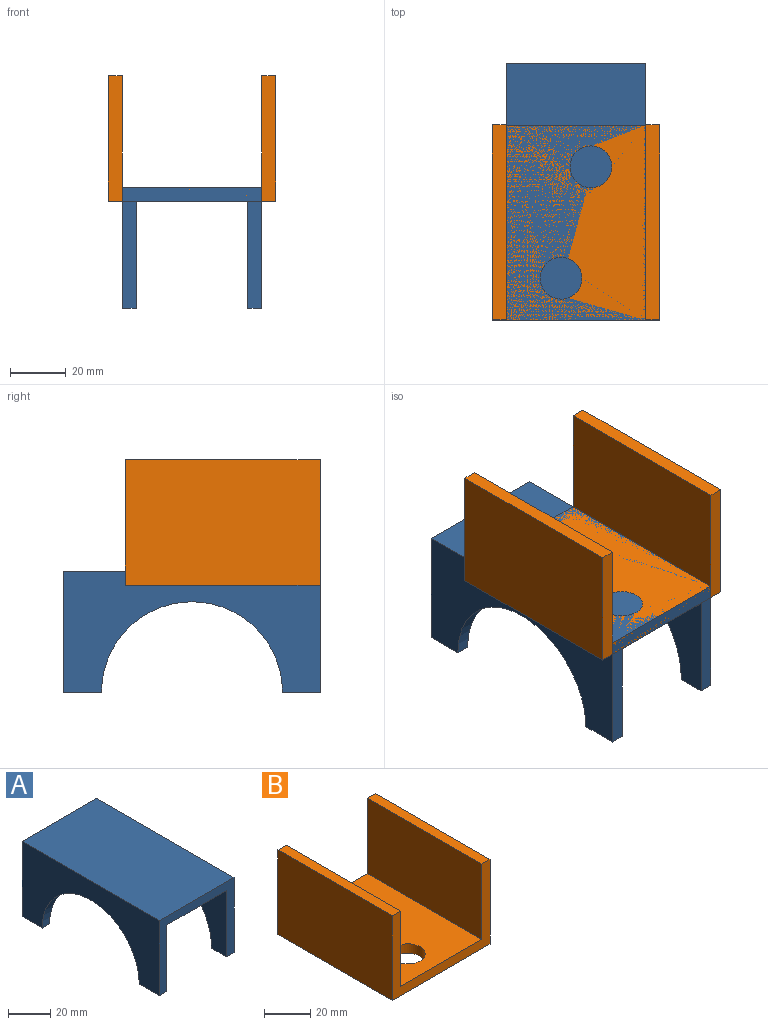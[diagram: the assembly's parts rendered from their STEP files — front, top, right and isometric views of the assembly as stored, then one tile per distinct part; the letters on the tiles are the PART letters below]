
ASSEMBLY  parts=2 mates=1
PART A: 14 faces, bbox 50x92x43.5 mm
  f0: plane 13.5x5mm, normal (0,0,-1), area 67.5mm2, adj f6,f8,f10,f13
  f1: plane 10x5mm, normal (0,0,-1), area 50mm2, adj f2,f3,f11,f12
  f2: plane 92x43.5mm, normal (1,0,0), area 1966.2mm2, adj f1,f4,f5,f10,f11,f12
  f3: plane 92x38.5mm, normal (-1,0,0), area 1506.2mm2, adj f1,f4,f9,f10,f11,f12
  f4: plane 10x5mm, normal (0,0,-1), area 50mm2, adj f2,f3,f10,f12
  f5: plane 92x50mm, normal (0,0,1), area 4600mm2, adj f2,f6,f10,f11
  f6: plane 92x43.5mm, normal (-1,0,0), area 2342.8mm2, adj f0,f5,f7,f10,f11,f13
  f7: plane 13.5x5mm, normal (0,0,-1), area 67.5mm2, adj f6,f8,f11,f13
  f8: plane 92x38.5mm, normal (1,0,0), area 1882.8mm2, adj f0,f7,f9,f10,f11,f13
  f9: plane 92x40mm, normal (0,0,-1), area 3680mm2, adj f3,f8,f10,f11
  f10: plane 50x43.5mm, normal (0,-1,0), area 635mm2, adj f0,f2,f3,f4,f5,f6,f8,f9
  f11: plane 50x43.5mm, normal (0,1,0), area 635mm2, adj f1,f2,f3,f5,f6,f7,f8,f9
  f12: cylinder r=36mm len=72mm, axis (1,0,0), area 565.5mm2, adj f1,f2,f3,f4
  f13: cylinder r=32.5mm len=65mm, axis (-1,0,0), area 510.5mm2, adj f0,f6,f7,f8
PART B: 12 faces, bbox 60x70x45 mm
  f0: plane 70x5mm, normal (0,0,1), area 350mm2, adj f1,f7,f8,f9
  f1: plane 70x40mm, normal (-1,0,0), area 2800mm2, adj f0,f2,f8,f9
  f2: plane 70x50mm, normal (0,0,1), area 3146.6mm2, adj f1,f3,f8,f9,f10,f11
  f3: plane 70x40mm, normal (1,0,0), area 2800mm2, adj f2,f4,f8,f9
  f4: plane 70x5mm, normal (0,0,1), area 350mm2, adj f3,f5,f8,f9
  f5: plane 70x45mm, normal (-1,0,0), area 3150mm2, adj f4,f6,f8,f9
  f6: plane 70x60mm, normal (0,0,-1), area 3846.6mm2, adj f5,f7,f8,f9,f10,f11
  f7: plane 70x45mm, normal (1,0,0), area 3150mm2, adj f0,f6,f8,f9
  f8: plane 60x45mm, normal (0,-1,0), area 700mm2, adj f0,f1,f2,f3,f4,f5,f6,f7
  f9: plane 60x45mm, normal (0,1,0), area 700mm2, adj f0,f1,f2,f3,f4,f5,f6,f7
  f10: cylinder r=7.5mm len=15mm, axis (0,0,1), area 235.6mm2, adj f2,f6
  f11: cylinder r=7.5mm len=15mm, axis (0,0,1), area 235.6mm2, adj f2,f6
PLACE A t=(-39.03,39.82,0.21)mm
PLACE B rot(axis=(0,-0.01,1),0deg) t=(-39.03,28.82,38.71)mm
MATE fastened B.f8 <-> A.f10  axis (0,-1,0) through (-39.03,-6.18,43.71)mm
